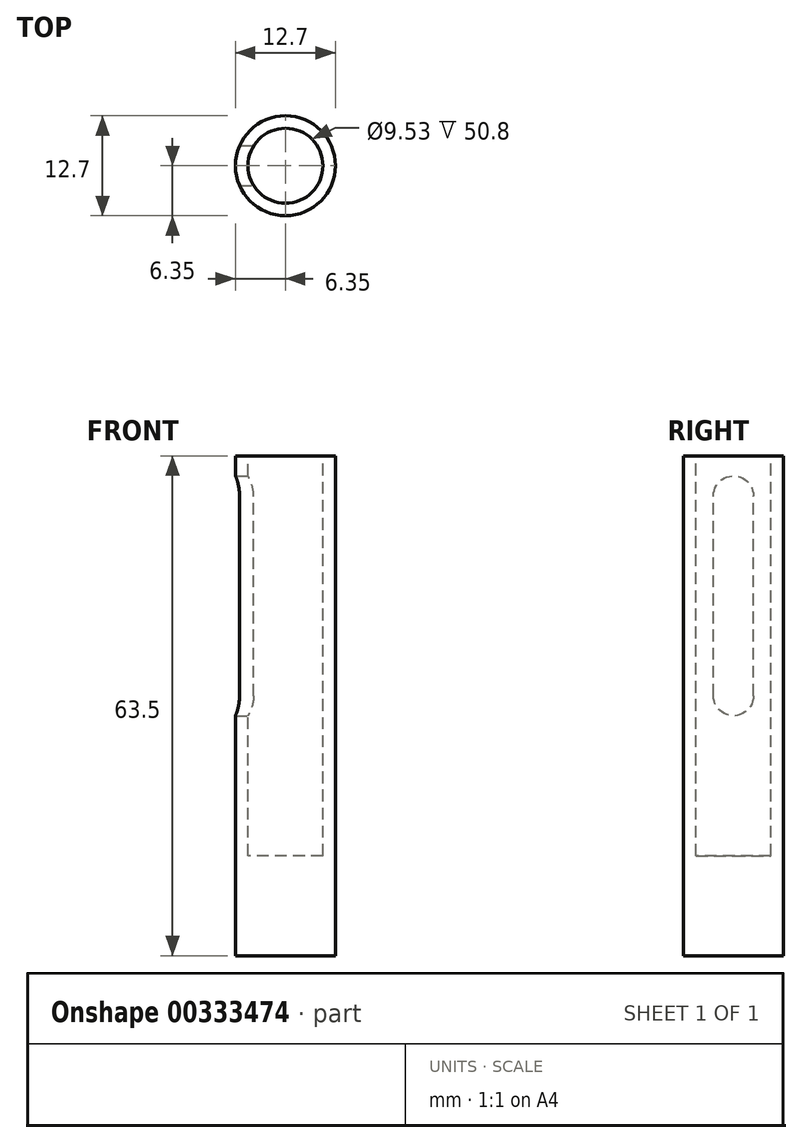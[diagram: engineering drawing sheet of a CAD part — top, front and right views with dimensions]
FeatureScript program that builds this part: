
annotation { "Feature Type Name" : "Feature", "Feature Type Description" : "" }
export const myFeature = defineFeature(function(context is Context, id is Id, definition is map)
    precondition{}
    {
        {
            var Q0;
            Q0=qCreatedBy(makeId("Top.planeOp"),FACE);
            var sketch = newSketch(context, id + "F0", { "sketchPlane" : qUnion([Q0])});
            skCircle(sketch, "E0", {"center": v(0, 0) * mm, "radius": 6.35 * mm});
            skCircle(sketch, "E1", {"center": v(0, 0) * mm, "radius": 4.76 * mm});
            skSolve(sketch);
        }
        {
            var Q0;
            Q0=makeQuery(id+"F0.imprint","IMPRINT",FACE,{"disambiguationData":[TD([[makeQuery(id+"F0.imprint","IMPRINT",EDGE,{"derivedFrom":sQuery(id+"F0.wireOp",EDGE,"E0")}),1.0]])]});
            var Q1;
            Q1=makeQuery(id+"F0.imprint","IMPRINT",FACE,{"disambiguationData":[TD([[makeQuery(id+"F0.imprint","IMPRINT",EDGE,{"derivedFrom":sQuery(id+"F0.wireOp",EDGE,"E1")}),1.0]])]});
            extrude(context, id + "F1", {"entities" : qUnion([Q0, Q1]), "oppositeDirection" : true, "depth" : 63.5 * mm});
        }
        {
            var Q0;
            Q0=makeQuery(id+"F0.imprint","IMPRINT",FACE,{"disambiguationData":[TD([[makeQuery(id+"F0.imprint","IMPRINT",EDGE,{"derivedFrom":sQuery(id+"F0.wireOp",EDGE,"E1")}),1.0]])]});
            extrude(context, id + "F2", {"entities" : qUnion([Q0]), "operationType" : NewBodyOperationType.REMOVE, "oppositeDirection" : true, "depth" : 50.8 * mm});
        }
        {
            var Q0;
            Q0=qCreatedBy(makeId("Right.planeOp"),FACE);
            var sketch = newSketch(context, id + "F3", { "sketchPlane" : qUnion([Q0])});
            skArc(sketch, "E2", {"start": v(2.54, -5.08) * mm, "mid": v(0, -2.54) * mm, "end": v(-2.54, -5.08) * mm});
            skArc(sketch, "E3", {"start": v(-2.54, -30.48) * mm, "mid": v(0, -33.02) * mm, "end": v(2.54, -30.48) * mm});
            skLineSegment(sketch, "E4", {"start": v(2.54, -5.08) * mm, "end": v(2.54, -30.48) * mm});
            skLineSegment(sketch, "E5", {"start": v(-2.54, -5.08) * mm, "end": v(-2.54, -30.48) * mm});
            skSolve(sketch);
        }
        {
            var Q0;
            Q0 = qSketchRegion(id + "F3", true);
            extrude(context, id + "F4", {"entities" : qUnion([Q0]), "operationType" : NewBodyOperationType.REMOVE, "oppositeDirection" : true, "depth" : 25.4 * mm});
        }
    });
